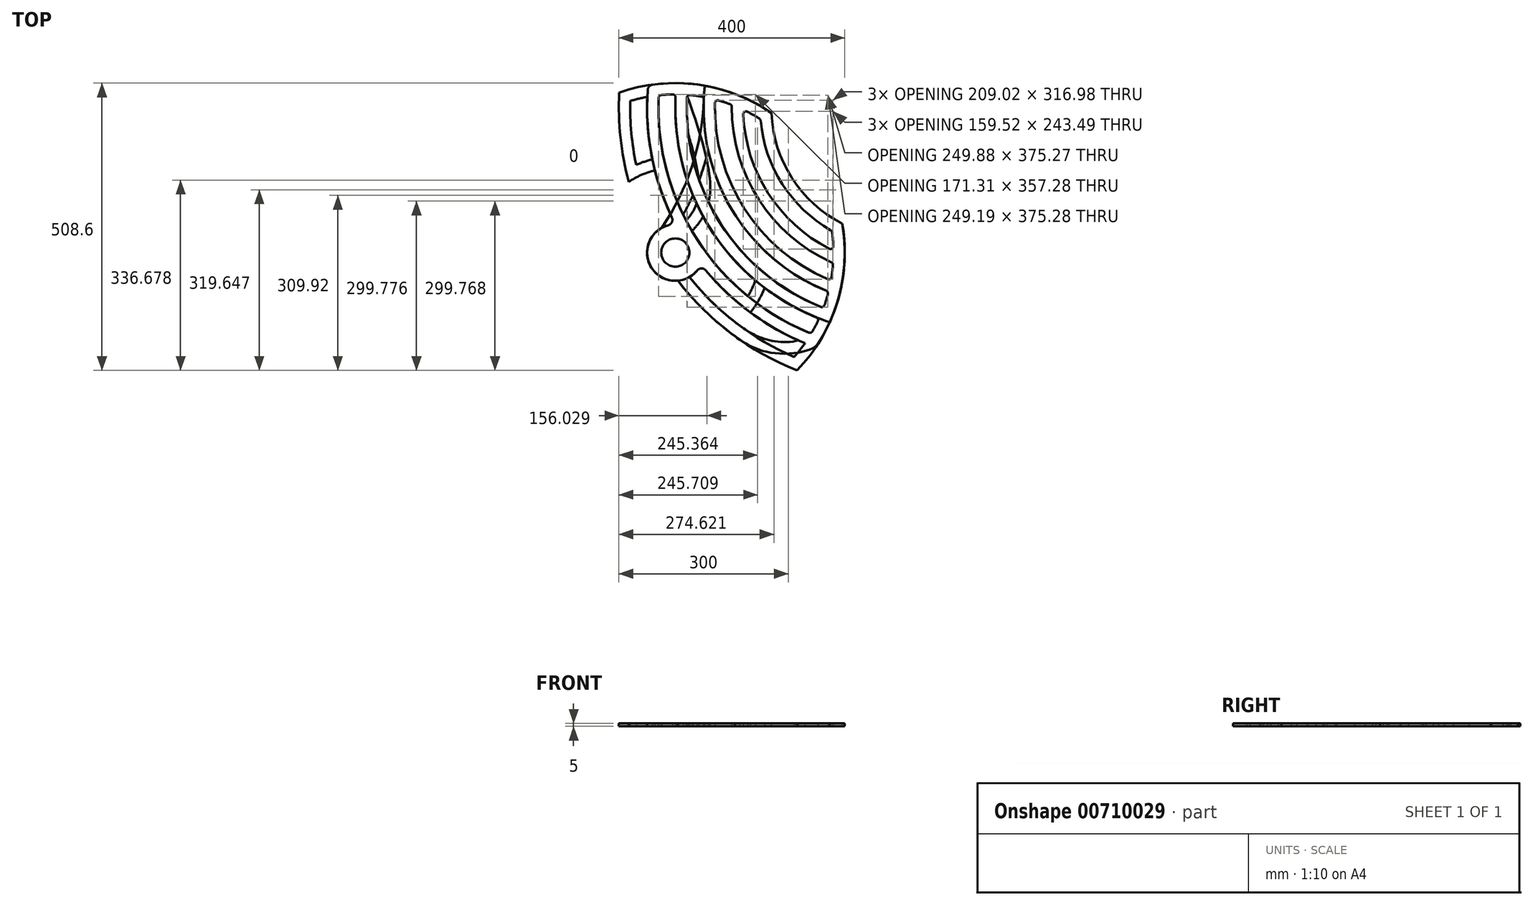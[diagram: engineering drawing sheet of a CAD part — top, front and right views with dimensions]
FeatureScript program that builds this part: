
annotation { "Feature Type Name" : "Feature", "Feature Type Description" : "" }
export const myFeature = defineFeature(function(context is Context, id is Id, definition is map)
    precondition{}
    {
        {
            var Q0;
            Q0=qCreatedBy(makeId("Top.planeOp"),FACE);
            var sketch = newSketch(context, id + "F0", { "sketchPlane" : qUnion([Q0])});
            skCircle(sketch, "E0", {"center": v(0, 0) * mm, "radius": 25 * mm});
            skArc(sketch, "E1", {"start": v(-48.22, 296.1) * mm, "mid": v(252.64, 161.79) * mm, "end": v(248.77, -167.67) * mm});
            skArc(sketch, "E2", {"start": v(0, 50) * mm, "mid": v(-42.1, -26.96) * mm, "end": v(45.41, -20.92) * mm});
            skLineSegment(sketch, "E3", {"start": v(-50, 340.96) * mm, "end": v(-50, -286.8) * mm, "construction": true});
            skLineSegment(sketch, "E4", {"start": v(-49.1, -31.44) * mm, "end": v(536.17, 343.36) * mm, "construction": true});
            skArc(sketch, "E5", {"start": v(-48.22, 296.1) * mm, "mid": v(-41.6, 169.62) * mm, "end": v(0, 50) * mm});
            skArc(sketch, "E6", {"start": v(-29.42, 278.45) * mm, "mid": v(-14.38, 279.63) * mm, "end": v(0.71, 280) * mm});
            skArc(sketch, "E7", {"start": v(-29.42, 278.45) * mm, "mid": v(37.89, 24.26) * mm, "end": v(240.6, -143.21) * mm});
            skArc(sketch, "E8.trimOffspring", {"start": v(45.41, -20.92) * mm, "mid": v(136.66, -108.75) * mm, "end": v(248.77, -167.67) * mm});
            skArc(sketch, "E9", {"start": v(0.71, 280) * mm, "mid": v(63.15, 40.44) * mm, "end": v(254.62, -116.49) * mm});
            skArc(sketch, "E10", {"start": v(20.7, 279.23) * mm, "mid": v(80, 51.23) * mm, "end": v(262.29, -98.01) * mm});
            skArc(sketch, "E11", {"start": v(50.53, 275.4) * mm, "mid": v(105.26, 67.4) * mm, "end": v(271.28, -69.32) * mm});
            skArc(sketch, "E12", {"start": v(70.34, 271.02) * mm, "mid": v(122.1, 78.2) * mm, "end": v(275.6, -49.5) * mm});
            skArc(sketch, "E13", {"start": v(100.05, 261.52) * mm, "mid": v(147.36, 94.37) * mm, "end": v(279.39, -18.53) * mm});
            skArc(sketch, "E14", {"start": v(120.02, 252.97) * mm, "mid": v(164.2, 105.16) * mm, "end": v(279.98, 3.18) * mm});
            skArc(sketch, "E15.trimOffspring", {"start": v(20.7, 279.23) * mm, "mid": v(35.67, 277.72) * mm, "end": v(50.53, 275.4) * mm});
            skArc(sketch, "E16.trimOffspring", {"start": v(70.34, 271.02) * mm, "mid": v(85.32, 266.68) * mm, "end": v(100.05, 261.52) * mm});
            skArc(sketch, "E17.trimOffspring", {"start": v(120.02, 252.97) * mm, "mid": v(135.69, 244.93) * mm, "end": v(150.82, 235.9) * mm});
            skArc(sketch, "E18.trimOffspring", {"start": v(279.39, -18.53) * mm, "mid": v(277.92, -34.07) * mm, "end": v(275.6, -49.5) * mm});
            skArc(sketch, "E19.trimOffspring", {"start": v(271.28, -69.32) * mm, "mid": v(267.17, -83.79) * mm, "end": v(262.29, -98.01) * mm});
            skArc(sketch, "E20.trimOffspring", {"start": v(254.62, -116.49) * mm, "mid": v(247.97, -130.04) * mm, "end": v(240.6, -143.21) * mm});
            skArc(sketch, "E21", {"start": v(150.82, 235.9) * mm, "mid": v(189.47, 121.33) * mm, "end": v(277.37, 38.3) * mm});
            skArc(sketch, "E22", {"start": v(172.81, 220.31) * mm, "mid": v(206.31, 132.12) * mm, "end": v(272.4, 64.8) * mm});
            skArc(sketch, "E23.trimOffspring", {"start": v(172.81, 220.31) * mm, "mid": v(235.8, 151) * mm, "end": v(272.4, 64.8) * mm});
            skArc(sketch, "E24.trimOffspring", {"start": v(277.37, 38.3) * mm, "mid": v(279.23, 20.78) * mm, "end": v(279.98, 3.18) * mm});
            skSolve(sketch);
        }
        {
            var Q0;
            Q0 = qSketchRegion(id + "F0", true);
            extrude(context, id + "F1", {"entities" : qUnion([Q0]), "depth" : 5 * mm, "offsetDistance" : 25 * mm});
        }
        {
            var Q0;
            Q0=makeQuery(id+"F1.opExtrude","SWEPT_EDGE",EDGE,{"disambiguationData":[OSD([sQuery(id+"F0.wireOp",EDGE,"E2"),sQuery(id+"F0.wireOp",EDGE,"E5")])]});
            var Q1;
            Q1=makeQuery(id+"F1.opExtrude","SWEPT_EDGE",EDGE,{"disambiguationData":[OSD([sQuery(id+"F0.wireOp",EDGE,"E2"),sQuery(id+"F0.wireOp",EDGE,"E8.trimOffspring")])]});
            var Q2;
            Q2=makeQuery(id+"F1.opExtrude","SWEPT_EDGE",EDGE,{"disambiguationData":[OSD([sQuery(id+"F0.wireOp",EDGE,"E1"),sQuery(id+"F0.wireOp",EDGE,"E8.trimOffspring")])]});
            var Q3;
            Q3=makeQuery(id+"F1.opExtrude","SWEPT_EDGE",EDGE,{"disambiguationData":[OSD([sQuery(id+"F0.wireOp",EDGE,"E1"),sQuery(id+"F0.wireOp",EDGE,"E5")])]});
            fillet(context, id + "F2", {"entities" : qUnion([Q0, Q1, Q2, Q3]), "radius" : 10 * mm, "tangentPropagation" : true, "allowEdgeOverflow" : false});
        }
        {
            var Q0;
            Q0=makeQuery(id+"F1.opExtrude","SWEPT_EDGE",EDGE,{"disambiguationData":[OSD([sQuery(id+"F0.wireOp",EDGE,"E6"),sQuery(id+"F0.wireOp",EDGE,"E7")])]});
            var Q1;
            Q1=makeQuery(id+"F1.opExtrude","SWEPT_EDGE",EDGE,{"disambiguationData":[OSD([sQuery(id+"F0.wireOp",EDGE,"E6"),sQuery(id+"F0.wireOp",EDGE,"E9")])]});
            var Q2;
            Q2=makeQuery(id+"F1.opExtrude","SWEPT_EDGE",EDGE,{"disambiguationData":[OSD([sQuery(id+"F0.wireOp",EDGE,"E11"),sQuery(id+"F0.wireOp",EDGE,"E15.trimOffspring")])]});
            var Q3;
            Q3=makeQuery(id+"F1.opExtrude","SWEPT_EDGE",EDGE,{"disambiguationData":[OSD([sQuery(id+"F0.wireOp",EDGE,"E10"),sQuery(id+"F0.wireOp",EDGE,"E15.trimOffspring")])]});
            var Q4;
            Q4=makeQuery(id+"F1.opExtrude","SWEPT_EDGE",EDGE,{"disambiguationData":[OSD([sQuery(id+"F0.wireOp",EDGE,"E12"),sQuery(id+"F0.wireOp",EDGE,"E16.trimOffspring")])]});
            var Q5;
            Q5=makeQuery(id+"F1.opExtrude","SWEPT_EDGE",EDGE,{"disambiguationData":[OSD([sQuery(id+"F0.wireOp",EDGE,"E14"),sQuery(id+"F0.wireOp",EDGE,"E17.trimOffspring")])]});
            var Q6;
            Q6=makeQuery(id+"F1.opExtrude","SWEPT_EDGE",EDGE,{"disambiguationData":[OSD([sQuery(id+"F0.wireOp",EDGE,"E13"),sQuery(id+"F0.wireOp",EDGE,"E16.trimOffspring")])]});
            var Q7;
            Q7=makeQuery(id+"F1.opExtrude","SWEPT_EDGE",EDGE,{"disambiguationData":[OSD([sQuery(id+"F0.wireOp",EDGE,"E17.trimOffspring"),sQuery(id+"F0.wireOp",EDGE,"E21")])]});
            var Q8;
            {var subQ0=sQuery(id+"F0.wireOp",EDGE,"E23.trimOffspring");var subQ1=sQuery(id+"F0.wireOp",EDGE,"E22");Q8=makeQuery(id+"F1.opExtrude","SWEPT_EDGE",EDGE,{"disambiguationData":[OSD([subQ1,subQ0]),TDD([makeQuery(id+"F0.imprint","INTERSECT",VERTEX,{"disambiguationData":[OD(0.0)],"derivedFrom":[subQ1,subQ0]})])]});}
            var Q9;
            {var subQ0=sQuery(id+"F0.wireOp",EDGE,"E23.trimOffspring");var subQ1=sQuery(id+"F0.wireOp",EDGE,"E22");Q9=makeQuery(id+"F1.opExtrude","SWEPT_EDGE",EDGE,{"disambiguationData":[OSD([subQ1,subQ0]),TDD([makeQuery(id+"F0.imprint","INTERSECT",VERTEX,{"disambiguationData":[OD(1.0)],"derivedFrom":[subQ1,subQ0]})])]});}
            var Q10;
            Q10=makeQuery(id+"F1.opExtrude","SWEPT_EDGE",EDGE,{"disambiguationData":[OSD([sQuery(id+"F0.wireOp",EDGE,"E14"),sQuery(id+"F0.wireOp",EDGE,"E24.trimOffspring")])]});
            var Q11;
            Q11=makeQuery(id+"F1.opExtrude","SWEPT_EDGE",EDGE,{"disambiguationData":[OSD([sQuery(id+"F0.wireOp",EDGE,"E12"),sQuery(id+"F0.wireOp",EDGE,"E18.trimOffspring")])]});
            var Q12;
            Q12=makeQuery(id+"F1.opExtrude","SWEPT_EDGE",EDGE,{"disambiguationData":[OSD([sQuery(id+"F0.wireOp",EDGE,"E10"),sQuery(id+"F0.wireOp",EDGE,"E19.trimOffspring")])]});
            var Q13;
            Q13=makeQuery(id+"F1.opExtrude","SWEPT_EDGE",EDGE,{"disambiguationData":[OSD([sQuery(id+"F0.wireOp",EDGE,"E21"),sQuery(id+"F0.wireOp",EDGE,"E24.trimOffspring")])]});
            var Q14;
            Q14=makeQuery(id+"F1.opExtrude","SWEPT_EDGE",EDGE,{"disambiguationData":[OSD([sQuery(id+"F0.wireOp",EDGE,"E13"),sQuery(id+"F0.wireOp",EDGE,"E18.trimOffspring")])]});
            var Q15;
            Q15=makeQuery(id+"F1.opExtrude","SWEPT_EDGE",EDGE,{"disambiguationData":[OSD([sQuery(id+"F0.wireOp",EDGE,"E11"),sQuery(id+"F0.wireOp",EDGE,"E19.trimOffspring")])]});
            var Q16;
            Q16=makeQuery(id+"F1.opExtrude","SWEPT_EDGE",EDGE,{"disambiguationData":[OSD([sQuery(id+"F0.wireOp",EDGE,"E9"),sQuery(id+"F0.wireOp",EDGE,"E20.trimOffspring")])]});
            var Q17;
            Q17=makeQuery(id+"F1.opExtrude","SWEPT_EDGE",EDGE,{"disambiguationData":[OSD([sQuery(id+"F0.wireOp",EDGE,"E7"),sQuery(id+"F0.wireOp",EDGE,"E20.trimOffspring")])]});
            fillet(context, id + "F3", {"entities" : qUnion([Q0, Q1, Q2, Q3, Q4, Q5, Q6, Q7, Q8, Q9, Q10, Q11, Q12, Q13, Q14, Q15, Q16, Q17]), "radius" : 5 * mm, "tangentPropagation" : true, "allowEdgeOverflow" : false});
        }
        {
            var Q0;
            Q0=qCreatedBy(makeId("Top.planeOp"),FACE);
            var sketch = newSketch(context, id + "F4", { "sketchPlane" : qUnion([Q0])});
            skCircle(sketch, "E25.0", {"center": v(0, 0) * mm, "radius": 25 * mm});
            skArc(sketch, "E26.0", {"start": v(2.4, 300) * mm, "mid": v(263.52, 143.38) * mm, "end": v(253.2, -160.91) * mm});
            skArc(sketch, "E27.0", {"start": v(-12.63, 48.38) * mm, "mid": v(-49.25, -8.61) * mm, "end": v(4.53, -49.8) * mm});
            skPoint(sketch, "E28.0", {"position": v(0.43, 274.73) * mm});
            skArc(sketch, "E29", {"start": v(0.43, 274.73) * mm, "mid": v(1.22, 287.38) * mm, "end": v(2.4, 300) * mm});
            skArc(sketch, "E30", {"start": v(24.9, -43.35) * mm, "mid": v(-15.07, 47.68) * mm, "end": v(4.53, -49.8) * mm, "construction": true});
            skArc(sketch, "E31.0", {"start": v(54.08, -31.66) * mm, "mid": v(128.87, -103) * mm, "end": v(217.96, -155.38) * mm});
            skArc(sketch, "E32.0", {"start": v(27.12, 42) * mm, "mid": v(116.57, -67.21) * mm, "end": v(236.57, -141.58) * mm});
            skArc(sketch, "E33", {"start": v(113.77, -129.17) * mm, "mid": v(66.57, -89.13) * mm, "end": v(24.9, -43.35) * mm});
            skArc(sketch, "E34", {"start": v(105.23, -147.71) * mm, "mid": v(51.43, -102.3) * mm, "end": v(4.53, -49.8) * mm});
            skFitSpline(sketch, "E35", {"points": [v(105.23, -147.71) * mm, v(171.2, -177.42) * mm, v(253.2, -160.91) * mm], "startDerivative": vector(99.59, -77.1) * mm, "endDerivative": vector(61.78, 88.77) * mm});
            skArc(sketch, "E36.0", {"start": v(252.34, -121.34) * mm, "mid": v(247.74, -130.48) * mm, "end": v(242.8, -139.44) * mm});
            skFitSpline(sketch, "E37", {"points": [v(113.77, -129.17) * mm, v(175.65, -157.09) * mm, v(242.8, -139.44) * mm], "startDerivative": vector(98.24, -71.15) * mm, "endDerivative": vector(67.14, 102.88) * mm});
            skPoint(sketch, "E38.0", {"position": v(46.35, -28.05) * mm});
            skArc(sketch, "E39.0", {"start": v(54.08, -31.66) * mm, "mid": v(46.35, -28.05) * mm, "end": v(38.66, -31.71) * mm});
            skArc(sketch, "E40.0.2", {"start": v(217.96, -155.38) * mm, "mid": v(128.87, -103) * mm, "end": v(54.08, -31.66) * mm});
            skArc(sketch, "E40.0.4", {"start": v(38.66, -31.71) * mm, "mid": v(32.31, -38.16) * mm, "end": v(24.9, -43.35) * mm});
            skArc(sketch, "E41.0", {"start": v(236.57, -141.58) * mm, "mid": v(240.1, -141.68) * mm, "end": v(242.8, -139.44) * mm});
            skArc(sketch, "E42.0", {"start": v(252.34, -121.34) * mm, "mid": v(252.5, -117.37) * mm, "end": v(249.71, -114.54) * mm});
            skArc(sketch, "E43.0.1", {"start": v(253.2, -160.91) * mm, "mid": v(252.67, -161.66) * mm, "end": v(252.07, -162.36) * mm});
            skArc(sketch, "E44.0", {"start": v(257.47, -96.1) * mm, "mid": v(261.4, -96.02) * mm, "end": v(264.06, -93.13) * mm});
            skArc(sketch, "E45.0", {"start": v(59, 88.45) * mm, "mid": v(141.23, -22.12) * mm, "end": v(257.47, -96.1) * mm});
            skArc(sketch, "E46.0", {"start": v(270.15, -73.62) * mm, "mid": v(267.28, -83.43) * mm, "end": v(264.06, -93.13) * mm});
            skArc(sketch, "E47.0", {"start": v(270.15, -73.62) * mm, "mid": v(269.8, -70.1) * mm, "end": v(267.22, -67.68) * mm});
            skArc(sketch, "E48.0", {"start": v(50.32, 271.03) * mm, "mid": v(105.26, 67.4) * mm, "end": v(267.22, -67.68) * mm});
            skArc(sketch, "E49.0", {"start": v(70.1, 264.67) * mm, "mid": v(122.1, 78.2) * mm, "end": v(269.73, -47.04) * mm});
            skArc(sketch, "E50.0", {"start": v(269.73, -47.04) * mm, "mid": v(274.12, -46.83) * mm, "end": v(276.64, -43.22) * mm});
            skArc(sketch, "E51.0", {"start": v(279.13, -22.06) * mm, "mid": v(278.09, -32.67) * mm, "end": v(276.64, -43.22) * mm});
            skPoint(sketch, "E52.0", {"position": v(278.45, -19.13) * mm});
            skArc(sketch, "E53.0", {"start": v(100, 258.04) * mm, "mid": v(147.36, 94.37) * mm, "end": v(276.2, -17.11) * mm});
            skArc(sketch, "E54.0", {"start": v(120.24, 244.62) * mm, "mid": v(164.2, 105.16) * mm, "end": v(272.49, 6.87) * mm});
            skArc(sketch, "E55.0", {"start": v(272.49, 6.87) * mm, "mid": v(277.46, 7.11) * mm, "end": v(279.76, 11.53) * mm});
            skArc(sketch, "E56.0", {"start": v(277.7, 35.82) * mm, "mid": v(279, 23.7) * mm, "end": v(279.76, 11.53) * mm});
            skArc(sketch, "E57.0", {"start": v(277.7, 35.82) * mm, "mid": v(276.9, 37.95) * mm, "end": v(275.24, 39.51) * mm});
            skArc(sketch, "E58.0", {"start": v(151.03, 233.46) * mm, "mid": v(189.47, 121.33) * mm, "end": v(275.24, 39.51) * mm});
            skArc(sketch, "E59.0", {"start": v(175.4, 206.58) * mm, "mid": v(206.31, 132.12) * mm, "end": v(261.01, 72.9) * mm});
            skArc(sketch, "E60.0", {"start": v(261.01, 72.9) * mm, "mid": v(266.87, 72.76) * mm, "end": v(268.83, 78.28) * mm});
            skArc(sketch, "E61.0", {"start": v(183.57, 211.43) * mm, "mid": v(235.8, 151) * mm, "end": v(268.83, 78.28) * mm});
            skArc(sketch, "E62.0", {"start": v(183.57, 211.43) * mm, "mid": v(177.73, 211.95) * mm, "end": v(175.4, 206.58) * mm});
            skArc(sketch, "E63.0", {"start": v(127.51, 249.28) * mm, "mid": v(138.24, 243.5) * mm, "end": v(148.7, 237.25) * mm});
            skArc(sketch, "E64.0", {"start": v(151.03, 233.46) * mm, "mid": v(150.31, 235.63) * mm, "end": v(148.7, 237.25) * mm});
            skArc(sketch, "E65.0", {"start": v(127.51, 249.28) * mm, "mid": v(122.54, 249.04) * mm, "end": v(120.24, 244.62) * mm});
            skArc(sketch, "E66.0", {"start": v(100, 258.04) * mm, "mid": v(99.12, 260.92) * mm, "end": v(96.73, 262.76) * mm});
            skArc(sketch, "E67.0", {"start": v(76.47, 269.35) * mm, "mid": v(86.67, 266.25) * mm, "end": v(96.73, 262.76) * mm});
            skArc(sketch, "E68.0", {"start": v(76.47, 269.35) * mm, "mid": v(72.15, 268.57) * mm, "end": v(70.1, 264.67) * mm});
            skArc(sketch, "E69.0", {"start": v(50.32, 271.03) * mm, "mid": v(49.2, 274.39) * mm, "end": v(46.14, 276.17) * mm});
            skArc(sketch, "E70.0", {"start": v(25.88, 278.8) * mm, "mid": v(36.04, 277.67) * mm, "end": v(46.14, 276.17) * mm});
            skArc(sketch, "E71.0", {"start": v(25.88, 278.8) * mm, "mid": v(22.14, 277.6) * mm, "end": v(20.42, 274.06) * mm});
            skPoint(sketch, "E72.orphan", {"position": v(241.23, -164.9) * mm});
            skPoint(sketch, "E73.0.7.start.orphan", {"position": v(-48.87, 288.1) * mm});
            skPoint(sketch, "E74.orphan", {"position": v(-40.23, 297.3) * mm});
            skPoint(sketch, "E75.0.end.orphan", {"position": v(-4.65, 279.96) * mm});
            skPoint(sketch, "E76.0.end.orphan", {"position": v(-29.63, 274.1) * mm});
            skPoint(sketch, "E76.0.start.orphan", {"position": v(-25.08, 278.87) * mm});
            skArc(sketch, "E77.trimOffspring", {"start": v(49.21, 63.94) * mm, "mid": v(134.05, -42.62) * mm, "end": v(249.71, -114.54) * mm});
            skPoint(sketch, "E73.0.6.start.orphan", {"position": v(-6.13, 62.36) * mm});
            skArc(sketch, "E78.trimOffspring", {"start": v(4.53, -49.8) * mm, "mid": v(-49.25, -8.61) * mm, "end": v(-12.63, 48.38) * mm});
            skArc(sketch, "E79.trimOffspring", {"start": v(24.9, -43.35) * mm, "mid": v(32.31, -38.16) * mm, "end": v(38.66, -31.71) * mm});
            skArc(sketch, "E80.0", {"start": v(279.13, -22.06) * mm, "mid": v(278.45, -19.13) * mm, "end": v(276.2, -17.11) * mm});
            skFitSpline(sketch, "E81", {"points": [v(12.04, 48.53) * mm, v(41.2, 102.55) * mm, v(0.43, 274.73) * mm], "startDerivative": vector(102.76, 114.93) * mm, "endDerivative": vector(-92.66, 255.03) * mm});
            skFitSpline(sketch, "E82.0", {"points": [v(26.95, 35.2) * mm, v(29.04, 37.54) * mm, v(33.5, 42.47) * mm, v(40.6, 50.91) * mm, v(46.45, 59.13) * mm, v(50.76, 66.58) * mm, v(53.73, 72.62) * mm, v(56.34, 79.13) * mm, v(58.15, 84.94) * mm, v(59.35, 89.8) * mm, v(60.11, 93.57) * mm, v(60.63, 96.8) * mm, v(60.98, 99.43) * mm, v(61.27, 102.1) * mm, v(61.55, 105.46) * mm, v(61.8, 110.92) * mm, v(61.8, 117.85) * mm, v(61.36, 126.38) * mm, v(60.5, 135.1) * mm, v(59.3, 144.02) * mm, v(57.27, 156.14) * mm, v(54, 171.66) * mm, v(49.16, 190.66) * mm, v(43.64, 209.8) * mm, v(37.66, 228.77) * mm, v(29.36, 253.48) * mm, v(23.1, 270.88) * mm, v(19.23, 281.56) * mm]});
            skArc(sketch, "E83", {"start": v(25.88, 278.8) * mm, "mid": v(22.97, 279.06) * mm, "end": v(20.06, 279.28) * mm});
            skArc(sketch, "E84", {"start": v(-12.63, 48.38) * mm, "mid": v(-0.3, 50) * mm, "end": v(12.04, 48.53) * mm});
            skPoint(sketch, "E85", {"position": v(30.74, 39.43) * mm});
            skFitSpline(sketch, "E86.trimOffspring", {"points": [v(26.95, 35.2) * mm, v(29.04, 37.54) * mm, v(33.5, 42.47) * mm, v(40.6, 50.91) * mm, v(46.45, 59.13) * mm, v(50.76, 66.58) * mm, v(53.73, 72.62) * mm, v(56.34, 79.13) * mm, v(58.15, 84.94) * mm, v(59.35, 89.8) * mm, v(60.11, 93.57) * mm, v(60.63, 96.8) * mm, v(60.98, 99.43) * mm, v(61.27, 102.1) * mm, v(61.55, 105.46) * mm, v(61.8, 110.92) * mm, v(61.8, 117.85) * mm, v(61.36, 126.38) * mm, v(60.5, 135.1) * mm, v(59.3, 144.02) * mm, v(57.27, 156.14) * mm, v(54, 171.66) * mm, v(49.16, 190.66) * mm, v(43.64, 209.8) * mm, v(37.66, 228.77) * mm, v(29.36, 253.48) * mm, v(23.1, 270.88) * mm, v(19.23, 281.56) * mm]});
            skSolve(sketch);
        }
        {
            var Q0;
            Q0 = qSketchRegion(id + "F4", true);
            extrude(context, id + "F5", {"entities" : qUnion([Q0]), "depth" : 5 * mm, "offsetDistance" : 25 * mm});
        }
        {
            var Q0;
            Q0 = qSketchRegion(id + "F4", true);
            extrude(context, id + "F6", {"entities" : qUnion([Q0]), "operationType" : NewBodyOperationType.ADD, "depth" : 5 * mm, "offsetDistance" : 25 * mm});
        }
        {
            var Q0;
            Q0=qCreatedBy(makeId("Top.planeOp"),FACE);
            var sketch = newSketch(context, id + "F7", { "sketchPlane" : qUnion([Q0])});
            skArc(sketch, "E87.0", {"start": v(175.4, 206.58) * mm, "mid": v(206.31, 132.12) * mm, "end": v(261.01, 72.9) * mm});
            skArc(sketch, "E88", {"start": v(210.36, -184.8) * mm, "mid": v(108.91, -125.5) * mm, "end": v(24.9, -43.35) * mm});
            skArc(sketch, "E89", {"start": v(215.6, -208.6) * mm, "mid": v(99.4, -143.39) * mm, "end": v(4.53, -49.8) * mm});
            skPoint(sketch, "E90.0", {"position": v(253.2, -160.91) * mm});
            skArc(sketch, "E91", {"start": v(253.2, -160.91) * mm, "mid": v(235.6, -185.7) * mm, "end": v(215.6, -208.6) * mm});
            skArc(sketch, "E92.0", {"start": v(-12.63, 48.38) * mm, "mid": v(-49.25, -8.61) * mm, "end": v(4.53, -49.8) * mm});
            skPoint(sketch, "E93.0", {"position": v(242.8, -139.44) * mm});
            skArc(sketch, "E94", {"start": v(229.56, -160.32) * mm, "mid": v(220.3, -172.82) * mm, "end": v(210.36, -184.8) * mm});
            skArc(sketch, "E95.0", {"start": v(54.08, -31.66) * mm, "mid": v(133.92, -106.75) * mm, "end": v(229.56, -160.32) * mm});
            skPoint(sketch, "E96.orphan", {"position": v(241.23, -164.9) * mm});
            skLineSegment(sketch, "E97", {"start": v(0, 0) * mm, "end": v(15.31, 402.68) * mm, "construction": true});
            skArc(sketch, "E98.0", {"start": v(-8.71, 67.86) * mm, "mid": v(-7.43, 65.1) * mm, "end": v(-6.13, 62.36) * mm, "construction": true});
            skArc(sketch, "E99.0", {"start": v(13.84, 67) * mm, "mid": v(106.08, -57.71) * mm, "end": v(236.57, -141.58) * mm});
            skArc(sketch, "E100.MirrorCS", {"start": v(50.35, 271.06) * mm, "mid": v(-35.94, 27.07) * mm, "end": v(-246.64, -123.2) * mm});
            skArc(sketch, "E101.MirrorCS", {"start": v(70.12, 264.88) * mm, "mid": v(70.11, 264.78) * mm, "end": v(70.1, 264.67) * mm});
            skPoint(sketch, "E102.0", {"position": v(50.32, 271.03) * mm});
            skPoint(sketch, "E103.0", {"position": v(70.1, 264.67) * mm});
            skArc(sketch, "E104.0", {"start": v(236.57, -141.58) * mm, "mid": v(240.1, -141.68) * mm, "end": v(242.8, -139.44) * mm});
            skArc(sketch, "E105.0", {"start": v(252.34, -121.34) * mm, "mid": v(247.74, -130.48) * mm, "end": v(242.8, -139.44) * mm});
            skArc(sketch, "E106.0", {"start": v(252.34, -121.34) * mm, "mid": v(252.5, -117.37) * mm, "end": v(249.71, -114.54) * mm});
            skArc(sketch, "E107.0", {"start": v(31.12, 101.46) * mm, "mid": v(118.85, -28.37) * mm, "end": v(249.71, -114.54) * mm});
            skArc(sketch, "E108.0", {"start": v(42.15, 128.31) * mm, "mid": v(125.8, -6.93) * mm, "end": v(257.47, -96.1) * mm});
            skArc(sketch, "E109.0", {"start": v(257.47, -96.1) * mm, "mid": v(261.4, -96.02) * mm, "end": v(264.06, -93.13) * mm});
            skArc(sketch, "E110.0", {"start": v(270.15, -73.62) * mm, "mid": v(267.28, -83.43) * mm, "end": v(264.06, -93.13) * mm});
            skArc(sketch, "E111.0", {"start": v(270.15, -73.62) * mm, "mid": v(269.8, -70.1) * mm, "end": v(267.22, -67.68) * mm});
            skArc(sketch, "E112.0", {"start": v(50.32, 271.03) * mm, "mid": v(50.2, 268.22) * mm, "end": v(50.12, 265.4) * mm});
            skArc(sketch, "E113.0", {"start": v(70.1, 264.67) * mm, "mid": v(122.1, 78.2) * mm, "end": v(269.73, -47.04) * mm});
            skArc(sketch, "E114.0", {"start": v(269.73, -47.04) * mm, "mid": v(274.12, -46.83) * mm, "end": v(276.64, -43.22) * mm});
            skArc(sketch, "E115.0", {"start": v(279.13, -22.06) * mm, "mid": v(278.09, -32.67) * mm, "end": v(276.64, -43.22) * mm});
            skArc(sketch, "E116.0", {"start": v(279.13, -22.06) * mm, "mid": v(278.45, -19.13) * mm, "end": v(276.2, -17.11) * mm});
            skArc(sketch, "E117.0", {"start": v(100, 258.04) * mm, "mid": v(147.36, 94.37) * mm, "end": v(276.2, -17.11) * mm});
            skArc(sketch, "E118.0", {"start": v(120.24, 244.62) * mm, "mid": v(164.2, 105.16) * mm, "end": v(272.49, 6.87) * mm});
            skArc(sketch, "E119.0", {"start": v(272.49, 6.87) * mm, "mid": v(277.46, 7.11) * mm, "end": v(279.76, 11.53) * mm});
            skArc(sketch, "E120.0", {"start": v(277.7, 35.82) * mm, "mid": v(279, 23.7) * mm, "end": v(279.76, 11.53) * mm});
            skArc(sketch, "E121.0", {"start": v(277.7, 35.82) * mm, "mid": v(276.9, 37.95) * mm, "end": v(275.24, 39.51) * mm});
            skArc(sketch, "E122.0", {"start": v(151.03, 233.46) * mm, "mid": v(189.47, 121.33) * mm, "end": v(275.24, 39.51) * mm});
            skArc(sketch, "E123.0", {"start": v(261.01, 72.9) * mm, "mid": v(266.87, 72.76) * mm, "end": v(268.83, 78.28) * mm});
            skArc(sketch, "E124.0", {"start": v(183.57, 211.43) * mm, "mid": v(235.8, 151) * mm, "end": v(268.83, 78.28) * mm});
            skArc(sketch, "E125.0", {"start": v(183.57, 211.43) * mm, "mid": v(177.73, 211.95) * mm, "end": v(175.4, 206.58) * mm});
            skArc(sketch, "E126.0", {"start": v(151.03, 233.46) * mm, "mid": v(150.31, 235.63) * mm, "end": v(148.7, 237.25) * mm});
            skArc(sketch, "E127.0", {"start": v(127.51, 249.28) * mm, "mid": v(138.24, 243.5) * mm, "end": v(148.7, 237.25) * mm});
            skArc(sketch, "E128.0", {"start": v(127.51, 249.28) * mm, "mid": v(122.54, 249.04) * mm, "end": v(120.24, 244.62) * mm});
            skArc(sketch, "E129.0", {"start": v(100, 258.04) * mm, "mid": v(99.12, 260.92) * mm, "end": v(96.73, 262.76) * mm});
            skArc(sketch, "E130.0", {"start": v(76.47, 269.35) * mm, "mid": v(86.67, 266.25) * mm, "end": v(96.73, 262.76) * mm});
            skArc(sketch, "E131.0", {"start": v(76.47, 269.35) * mm, "mid": v(72.15, 268.57) * mm, "end": v(70.1, 264.67) * mm});
            skArc(sketch, "E132.0", {"start": v(52.24, 295.42) * mm, "mid": v(274.56, 120.9) * mm, "end": v(253.2, -160.91) * mm});
            skArc(sketch, "E133.0", {"start": v(54.08, -31.66) * mm, "mid": v(46.35, -28.05) * mm, "end": v(38.66, -31.71) * mm});
            skPoint(sketch, "E134.orphan", {"position": v(-48.87, 288.1) * mm});
            skArc(sketch, "E135", {"start": v(50.35, 271.06) * mm, "mid": v(51.09, 283.26) * mm, "end": v(52.24, 295.42) * mm});
            skPoint(sketch, "E136.0.end.orphan", {"position": v(-29.63, 274.1) * mm});
            skPoint(sketch, "E137.orphan", {"position": v(-40.23, 297.3) * mm});
            skPoint(sketch, "E138.0.end.orphan", {"position": v(46.14, 276.17) * mm});
            skPoint(sketch, "E139.0.start.orphan", {"position": v(25.88, 278.8) * mm});
            skPoint(sketch, "E140.orphan", {"position": v(20.42, 274.06) * mm});
            skPoint(sketch, "E141.0.start.orphan", {"position": v(-25.08, 278.87) * mm});
            skPoint(sketch, "E142.0.end.orphan", {"position": v(-4.65, 279.96) * mm});
            skPoint(sketch, "E143.orphan", {"position": v(0.43, 274.73) * mm});
            skPoint(sketch, "E144.orphan", {"position": v(70.6, 283.55) * mm});
            skArc(sketch, "E145.trimOffspring", {"start": v(58.2, 180.85) * mm, "mid": v(50.98, 154.33) * mm, "end": v(42.15, 128.31) * mm});
            skArc(sketch, "E146.trimOffspring", {"start": v(58.2, 180.85) * mm, "mid": v(132.14, 30.87) * mm, "end": v(267.22, -67.68) * mm});
            skArc(sketch, "E147.trimOffspring", {"start": v(31.12, 101.46) * mm, "mid": v(22.85, 84.05) * mm, "end": v(13.84, 67) * mm});
            skPoint(sketch, "E148.orphan", {"position": v(10.85, 61.71) * mm});
            skArc(sketch, "E149.trimOffspring", {"start": v(24.9, -43.35) * mm, "mid": v(32.31, -38.16) * mm, "end": v(38.66, -31.71) * mm});
            skCircle(sketch, "E150.0", {"center": v(0, 0) * mm, "radius": 25 * mm});
            skSolve(sketch);
        }
        {
            var Q0;
            Q0 = qSketchRegion(id + "F7", true);
            extrude(context, id + "F8", {"entities" : qUnion([Q0]), "depth" : 5 * mm, "offsetDistance" : 25 * mm});
        }
        {
            var Q0;
            Q0=qCreatedBy(makeId("Top.planeOp"),FACE);
            var sketch = newSketch(context, id + "F9", { "sketchPlane" : qUnion([Q0])});
            skArc(sketch, "E151.0", {"start": v(-40.23, 297.3) * mm, "mid": v(240.47, 179.37) * mm, "end": v(273.49, -123.31) * mm});
            skArc(sketch, "E152.0", {"start": v(-49.58, 275.58) * mm, "mid": v(-48.55, 220.04) * mm, "end": v(-40.68, 165.06) * mm});
            skArc(sketch, "E153.0", {"start": v(-29.63, 274.1) * mm, "mid": v(7.88, 79.68) * mm, "end": v(128.54, -77.32) * mm});
            skArc(sketch, "E154", {"start": v(-79.84, 268.37) * mm, "mid": v(-77.92, 211.5) * mm, "end": v(-69.27, 155.25) * mm});
            skArc(sketch, "E155", {"start": v(-99.27, 283.1) * mm, "mid": v(-97.22, 203.5) * mm, "end": v(-82.56, 125.24) * mm});
            skArc(sketch, "E156", {"start": v(-40.23, 297.3) * mm, "mid": v(-70.11, 291.7) * mm, "end": v(-99.27, 283.1) * mm});
            skArc(sketch, "E157.0", {"start": v(-12.63, 48.38) * mm, "mid": v(-42.1, -26.96) * mm, "end": v(38.66, -31.71) * mm});
            skArc(sketch, "E158", {"start": v(-82.56, 125.24) * mm, "mid": v(-60.24, 137.37) * mm, "end": v(-36.2, 145.57) * mm});
            skArc(sketch, "E159", {"start": v(-69.27, 155.25) * mm, "mid": v(-55.2, 160.79) * mm, "end": v(-40.68, 165.06) * mm});
            skPoint(sketch, "E160.0", {"position": v(-25.08, 278.87) * mm});
            skArc(sketch, "E161", {"start": v(-49.58, 275.58) * mm, "mid": v(-64.81, 272.4) * mm, "end": v(-79.84, 268.37) * mm});
            skArc(sketch, "E162.0.0", {"start": v(54.08, -31.66) * mm, "mid": v(91.24, -71.21) * mm, "end": v(132.9, -106) * mm});
            skArc(sketch, "E162.0.2", {"start": v(273.49, -123.31) * mm, "mid": v(240.47, 179.37) * mm, "end": v(-40.23, 297.3) * mm});
            skArc(sketch, "E162.0.5", {"start": v(-6.13, 62.36) * mm, "mid": v(-6.09, 53.84) * mm, "end": v(-12.63, 48.38) * mm});
            skArc(sketch, "E162.0.7", {"start": v(38.66, -31.71) * mm, "mid": v(46.35, -28.05) * mm, "end": v(54.08, -31.66) * mm});
            skArc(sketch, "E163.0.2", {"start": v(132.9, -106) * mm, "mid": v(91.24, -71.21) * mm, "end": v(54.08, -31.66) * mm});
            skArc(sketch, "E163.0.3", {"start": v(54.08, -31.66) * mm, "mid": v(46.35, -28.05) * mm, "end": v(38.66, -31.71) * mm});
            skArc(sketch, "E163.0.4", {"start": v(38.66, -31.71) * mm, "mid": v(-42.1, -26.96) * mm, "end": v(-12.63, 48.38) * mm});
            skArc(sketch, "E163.0.5", {"start": v(-12.63, 48.38) * mm, "mid": v(-6.09, 53.84) * mm, "end": v(-6.13, 62.36) * mm});
            skArc(sketch, "E163.0.6", {"start": v(-6.13, 62.36) * mm, "mid": v(-23.22, 103.22) * mm, "end": v(-36.2, 145.57) * mm});
            skCircle(sketch, "E164", {"center": v(0, 0) * mm, "radius": 25 * mm});
            skArc(sketch, "E165", {"start": v(0.43, 274.73) * mm, "mid": v(33.33, 96.3) * mm, "end": v(141.68, -49.25) * mm});
            skArc(sketch, "E166", {"start": v(0.43, 274.73) * mm, "mid": v(-0.98, 278.44) * mm, "end": v(-4.65, 279.96) * mm});
            skArc(sketch, "E167", {"start": v(-25.08, 278.87) * mm, "mid": v(-14.87, 279.6) * mm, "end": v(-4.65, 279.96) * mm});
            skArc(sketch, "E168", {"start": v(-25.08, 278.87) * mm, "mid": v(-28.25, 277.34) * mm, "end": v(-29.63, 274.1) * mm});
            skArc(sketch, "E169", {"start": v(25.88, 278.8) * mm, "mid": v(36.04, 277.67) * mm, "end": v(46.14, 276.17) * mm});
            skArc(sketch, "E170", {"start": v(25.88, 278.8) * mm, "mid": v(22.14, 277.6) * mm, "end": v(20.42, 274.06) * mm});
            skArc(sketch, "E171", {"start": v(20.42, 274.06) * mm, "mid": v(80, 51.23) * mm, "end": v(257.47, -96.1) * mm});
            skArc(sketch, "E172", {"start": v(257.47, -96.1) * mm, "mid": v(261.4, -96.02) * mm, "end": v(264.06, -93.13) * mm});
            skArc(sketch, "E173", {"start": v(270.15, -73.62) * mm, "mid": v(267.28, -83.43) * mm, "end": v(264.06, -93.13) * mm});
            skArc(sketch, "E174", {"start": v(270.15, -73.62) * mm, "mid": v(269.8, -70.1) * mm, "end": v(267.22, -67.68) * mm});
            skArc(sketch, "E175", {"start": v(50.32, 271.03) * mm, "mid": v(105.26, 67.4) * mm, "end": v(267.22, -67.68) * mm});
            skArc(sketch, "E176", {"start": v(50.32, 271.03) * mm, "mid": v(49.2, 274.39) * mm, "end": v(46.14, 276.17) * mm});
            skArc(sketch, "E177", {"start": v(76.47, 269.35) * mm, "mid": v(86.67, 266.25) * mm, "end": v(96.73, 262.76) * mm});
            skArc(sketch, "E178", {"start": v(76.47, 269.35) * mm, "mid": v(72.15, 268.57) * mm, "end": v(70.1, 264.67) * mm});
            skArc(sketch, "E179", {"start": v(70.1, 264.67) * mm, "mid": v(122.1, 78.2) * mm, "end": v(269.73, -47.04) * mm});
            skArc(sketch, "E180", {"start": v(269.73, -47.04) * mm, "mid": v(274.12, -46.83) * mm, "end": v(276.64, -43.22) * mm});
            skArc(sketch, "E181", {"start": v(279.13, -22.06) * mm, "mid": v(278.09, -32.67) * mm, "end": v(276.64, -43.22) * mm});
            skArc(sketch, "E182", {"start": v(279.13, -22.06) * mm, "mid": v(278.45, -19.13) * mm, "end": v(276.2, -17.11) * mm});
            skArc(sketch, "E183", {"start": v(100, 258.04) * mm, "mid": v(147.36, 94.37) * mm, "end": v(276.2, -17.11) * mm});
            skArc(sketch, "E184", {"start": v(100, 258.04) * mm, "mid": v(99.12, 260.92) * mm, "end": v(96.73, 262.76) * mm});
            skArc(sketch, "E185", {"start": v(151.03, 233.46) * mm, "mid": v(189.47, 121.33) * mm, "end": v(275.24, 39.51) * mm});
            skArc(sketch, "E186", {"start": v(151.03, 233.46) * mm, "mid": v(150.31, 235.63) * mm, "end": v(148.7, 237.25) * mm});
            skArc(sketch, "E187", {"start": v(127.51, 249.28) * mm, "mid": v(138.24, 243.5) * mm, "end": v(148.7, 237.25) * mm});
            skArc(sketch, "E188", {"start": v(127.51, 249.28) * mm, "mid": v(122.54, 249.04) * mm, "end": v(120.24, 244.62) * mm});
            skArc(sketch, "E189", {"start": v(120.24, 244.62) * mm, "mid": v(164.2, 105.16) * mm, "end": v(272.49, 6.87) * mm});
            skArc(sketch, "E190", {"start": v(272.49, 6.87) * mm, "mid": v(277.46, 7.11) * mm, "end": v(279.76, 11.53) * mm});
            skArc(sketch, "E191", {"start": v(277.7, 35.82) * mm, "mid": v(279, 23.7) * mm, "end": v(279.76, 11.53) * mm});
            skArc(sketch, "E192", {"start": v(277.7, 35.82) * mm, "mid": v(276.9, 37.95) * mm, "end": v(275.24, 39.51) * mm});
            skArc(sketch, "E193", {"start": v(183.57, 211.43) * mm, "mid": v(235.8, 151) * mm, "end": v(268.83, 78.28) * mm});
            skArc(sketch, "E194", {"start": v(183.57, 211.43) * mm, "mid": v(177.73, 211.95) * mm, "end": v(175.4, 206.58) * mm});
            skArc(sketch, "E195", {"start": v(175.4, 206.58) * mm, "mid": v(206.31, 132.12) * mm, "end": v(261.01, 72.9) * mm});
            skArc(sketch, "E196", {"start": v(261.01, 72.9) * mm, "mid": v(266.87, 72.76) * mm, "end": v(268.83, 78.28) * mm});
            skArc(sketch, "E197", {"start": v(128.54, -77.32) * mm, "mid": v(135.84, -63.63) * mm, "end": v(141.68, -49.25) * mm});
            skArc(sketch, "E198", {"start": v(132.9, -106) * mm, "mid": v(147.13, -85.15) * mm, "end": v(158.12, -62.43) * mm});
            skArc(sketch, "E199", {"start": v(249.71, -114.54) * mm, "mid": v(261.53, -119.11) * mm, "end": v(273.49, -123.31) * mm});
            skPoint(sketch, "E200.orphan", {"position": v(241.23, -164.9) * mm});
            skPoint(sketch, "E201.trimOffspring.end.orphan", {"position": v(236.57, -141.58) * mm});
            skArc(sketch, "E202.trimOffspring", {"start": v(158.12, -62.43) * mm, "mid": v(202.2, -91.51) * mm, "end": v(249.71, -114.54) * mm});
            skArc(sketch, "E203.trimOffspring", {"start": v(-40.68, 165.06) * mm, "mid": v(-48.55, 220.04) * mm, "end": v(-49.58, 275.58) * mm});
            skArc(sketch, "E204.trimOffspring", {"start": v(-36.2, 145.57) * mm, "mid": v(-23.22, 103.22) * mm, "end": v(-6.13, 62.36) * mm});
            skSolve(sketch);
        }
        {
            var Q0;
            Q0 = qSketchRegion(id + "F9", true);
            extrude(context, id + "F10", {"entities" : qUnion([Q0]), "depth" : 5 * mm, "offsetDistance" : 25 * mm});
        }
        {
            var Q0;
            Q0=makeQuery(id+"F8.opExtrude","CAP_FACE",FACE,{"disambiguationData":[OSD([sQuery(id+"F7.wireOp",EDGE,"E87.0"),sQuery(id+"F7.wireOp",EDGE,"E88"),sQuery(id+"F7.wireOp",EDGE,"E89"),sQuery(id+"F7.wireOp",EDGE,"E91"),sQuery(id+"F7.wireOp",EDGE,"E92.0"),sQuery(id+"F7.wireOp",EDGE,"E94"),sQuery(id+"F7.wireOp",EDGE,"E95.0"),sQuery(id+"F7.wireOp",EDGE,"E99.0"),sQuery(id+"F7.wireOp",EDGE,"E100.MirrorCS"),sQuery(id+"F7.wireOp",EDGE,"E104.0"),sQuery(id+"F7.wireOp",EDGE,"E105.0"),sQuery(id+"F7.wireOp",EDGE,"E106.0"),sQuery(id+"F7.wireOp",EDGE,"E107.0"),sQuery(id+"F7.wireOp",EDGE,"E108.0"),sQuery(id+"F7.wireOp",EDGE,"E109.0"),sQuery(id+"F7.wireOp",EDGE,"E110.0"),sQuery(id+"F7.wireOp",EDGE,"E111.0"),sQuery(id+"F7.wireOp",EDGE,"E113.0"),sQuery(id+"F7.wireOp",EDGE,"E114.0"),sQuery(id+"F7.wireOp",EDGE,"E115.0"),sQuery(id+"F7.wireOp",EDGE,"E116.0"),sQuery(id+"F7.wireOp",EDGE,"E117.0"),sQuery(id+"F7.wireOp",EDGE,"E118.0"),sQuery(id+"F7.wireOp",EDGE,"E119.0"),sQuery(id+"F7.wireOp",EDGE,"E120.0"),sQuery(id+"F7.wireOp",EDGE,"E121.0"),sQuery(id+"F7.wireOp",EDGE,"E122.0"),sQuery(id+"F7.wireOp",EDGE,"E123.0"),sQuery(id+"F7.wireOp",EDGE,"E124.0"),sQuery(id+"F7.wireOp",EDGE,"E125.0"),sQuery(id+"F7.wireOp",EDGE,"E126.0"),sQuery(id+"F7.wireOp",EDGE,"E127.0"),sQuery(id+"F7.wireOp",EDGE,"E128.0"),sQuery(id+"F7.wireOp",EDGE,"E129.0"),sQuery(id+"F7.wireOp",EDGE,"E130.0"),sQuery(id+"F7.wireOp",EDGE,"E131.0"),sQuery(id+"F7.wireOp",EDGE,"E132.0"),sQuery(id+"F7.wireOp",EDGE,"E133.0"),sQuery(id+"F7.wireOp",EDGE,"E135"),sQuery(id+"F7.wireOp",EDGE,"E145.trimOffspring"),sQuery(id+"F7.wireOp",EDGE,"E146.trimOffspring"),sQuery(id+"F7.wireOp",EDGE,"E147.trimOffspring"),sQuery(id+"F7.wireOp",EDGE,"E149.trimOffspring"),sQuery(id+"F7.wireOp",EDGE,"E150.0")])],"isStart":false});
            var sketch = newSketch(context, id + "F11", { "sketchPlane" : qUnion([Q0])});
            skArc(sketch, "E205.0", {"start": v(175.4, 206.58) * mm, "mid": v(206.31, 132.12) * mm, "end": v(261.01, 72.9) * mm});
            skCircle(sketch, "E206", {"center": v(400, 256.16) * mm, "radius": 230 * mm});
            skSolve(sketch);
        }
        {
            var Q0;
            {var subQ1=makeQuery(id+"F8.opExtrude","CAP_EDGE",EDGE,{"disambiguationData":[OSD([sQuery(id+"F7.wireOp",EDGE,"E123.0")])],"isStart":false});var subQ2=makeQuery(id+"F11.imprint","IMPRINT",EDGE,{"derivedFrom":subQ1});var subQ3=sQuery(id+"F11.wireOp",EDGE,"E206");var subQ4=sQuery(id+"F11.wireOp",EDGE,"E205.0");var subQ5=makeQuery(id+"F8.opExtrude","CAP_EDGE",EDGE,{"disambiguationData":[OSD([sQuery(id+"F7.wireOp",EDGE,"E91"),sQuery(id+"F7.wireOp",EDGE,"E132.0")])],"isStart":false});var subQ8=makeQuery(id+"F11.imprint","INTERSECT",VERTEX,{"disambiguationData":[OD(0.0)],"derivedFrom":[subQ5,subQ3]});Q0=qUnion([makeQuery(id+"F11.imprint","IMPRINT",FACE,{"disambiguationData":[TD([[makeQuery(id+"F11.imprint","IMPRINT",EDGE,{"derivedFrom":subQ4}),1.0]])]}),makeQuery(id+"F11.imprint","IMPRINT",FACE,{"disambiguationData":[TD([[makeQuery(id+"F11.imprint","IMPRINT",EDGE,{"disambiguationData":[TD([[subQ8,1.0]])],"derivedFrom":subQ3}),1.0]])]}),makeQuery(id+"F11.imprint","IMPRINT",FACE,{"disambiguationData":[TD([[subQ2,-1.0]])]})]);}
            extrude(context, id + "F12", {"entities" : qUnion([Q0]), "operationType" : NewBodyOperationType.REMOVE, "endBound" : BoundingType.THROUGH_ALL, "oppositeDirection" : true, "depth" : 25 * mm, "offsetDistance" : 25 * mm});
        }
    });
